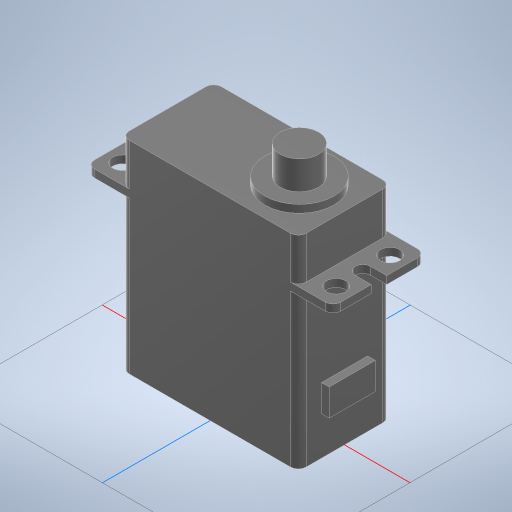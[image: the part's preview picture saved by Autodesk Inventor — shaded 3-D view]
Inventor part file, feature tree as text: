
AUTODESK INVENTOR PART (.ipt)
format: ipt  version: 2023 (Build 270158000, 158)  size: 519,680 bytes
history: native  units: mm
features: extrude x11, sketch x6, other x2, fillet x1, mirror x1, plane x1
ambient origin geometry x8: Origin, YZ Plane, XZ Plane, XY Plane, X Axis, Y Axis, Z Axis, Center Point
bodies: Solid1 (feature_tree)
feature tree (22):
  sketch  "Sketch1"  dims[d19=23.0mm d30=32.0mm]
  sketch  "Sketch5"  dims[d42=12.0mm d43=23.0mm]
  sketch  "Sketch6"  dims[d44=12.0mm d45=26.3mm d46=0.0mm]
  extrude  "Extrusion1"  Depth=32.0mm
  extrude  "Extrusion2"  Depth=23.0mm
  extrude  "Extrusion3"  Depth=26.3mm TaperAngle=0.0deg
  extrude  "Extrusion4"  Depth=19.8mm
  extrude  "Extrusion5"  Depth=4.5mm TaperAngle=0.0deg
  fillet  "Fillet1"  Radius=19.8mm
  extrude  "Extrusion6"  Depth=4.5mm TaperAngle=0.0deg
  extrude  "Extrusion7"  Depth=10.0mm
  extrude  "Extrusion8"  Depth=5.0mm
  extrude  "Extrusion9"  Depth=3.7mm TaperAngle=0.0deg
  extrude  "Extrusion10"  Depth=1.0mm
  extrude  "Extrusion11"  Depth=2.5mm
  mirror  "Spiegeln1"
  other  "Image1"
  other  "Image4"
  sketch  "Sketch7"  dims[d47=1.0mm d48=0.0mm d49=19.8mm]
  sketch  "Sketch8"  dims[d50=1.0mm d51=4.5mm d52=0.0mm d53=19.8mm]
  sketch  "Sketch9"  dims[d54=1.0mm d55=4.5mm d56=0.0mm d57=9.0mm d58=5.0mm d59=3.7mm d60=0.0mm d61=1.0mm d63=2.5mm d68=3.7mm d69=0.0mm d70=10.0mm d71=0.0mm d72=10.0mm d73=0.0mm d74=10.0mm d75=0.0mm d76=26.3mm d77=5.0mm d78=3.5mm d79=3.0mm d80=1.0mm d81=0.0mm d83=2.0mm d84=1.0mm d86=10.0mm d87=0.0mm d62=0.872665mm d88=0.5mm d89=0.872665mm]
  plane  "Arbeitsebene1"
